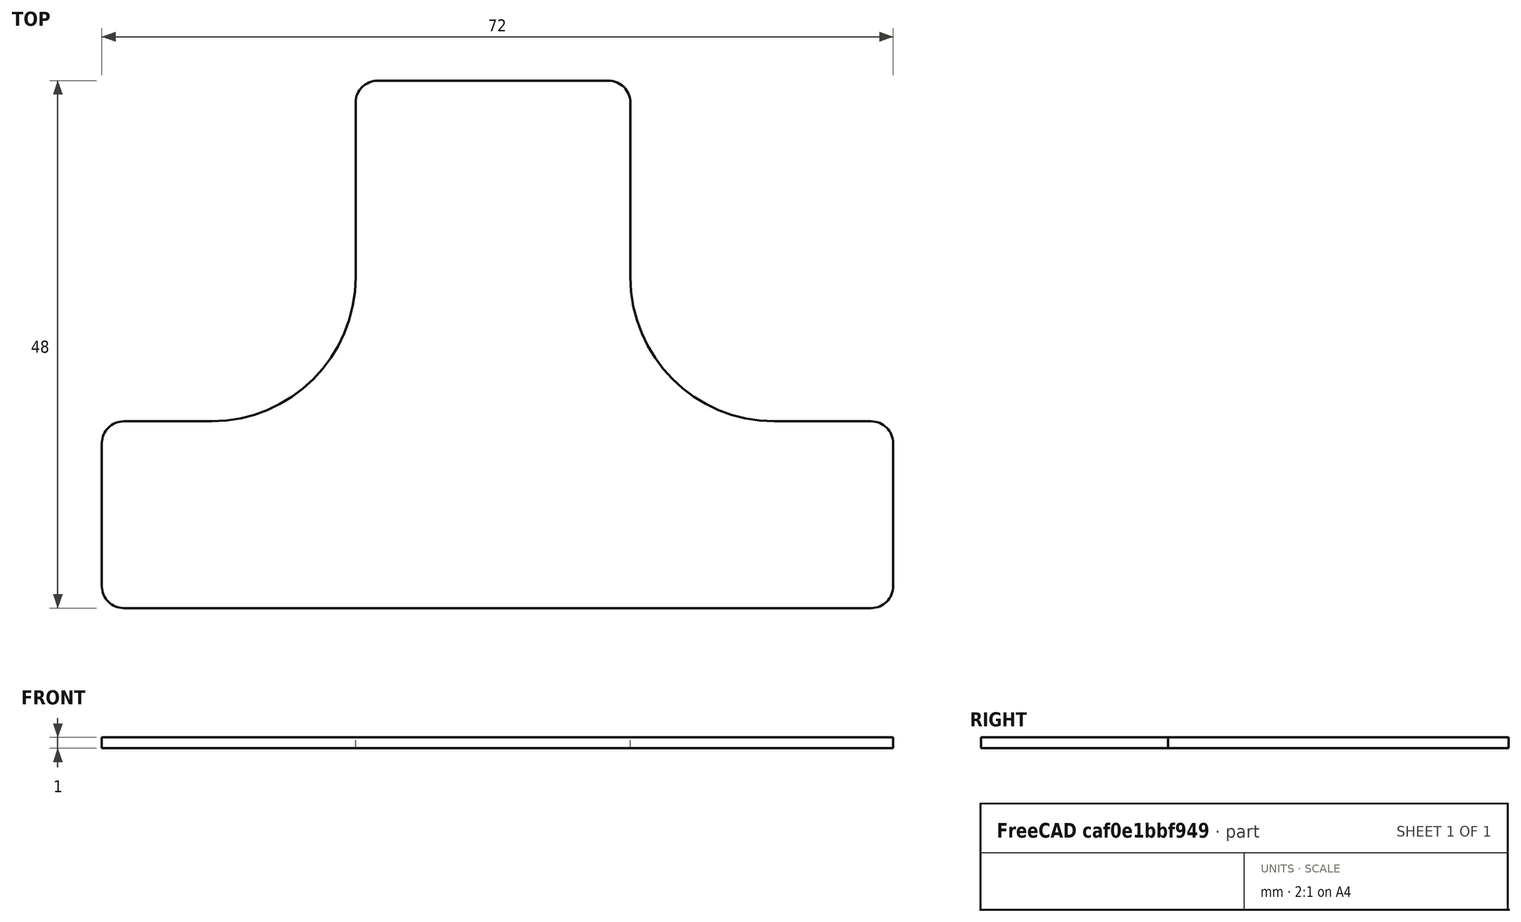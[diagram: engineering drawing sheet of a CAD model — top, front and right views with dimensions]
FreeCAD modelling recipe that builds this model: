
FCSTD DOCUMENT  (FreeCAD 0.16R6712 (Git))
Label: Me_LineFolloweArray
License: All rights reserved
LicenseURL: http://en.wikipedia.org/wiki/All_rights_reserved
objects: Sketcher::SketchObject×1, PartDesign::Pad×1
note: 3 computed .brp shape members not serialized (recipe doc carries the construction recipe); baked Part::Feature solids carry a one-line shape summary decoded from their .brp

FEATURE [Sketcher::SketchObject] Sketch
  sketch-geometry (16):
    g0: LineSegment StartX=-33.5897 StartY=-18.8788 StartZ=0 EndX=34.4103 EndY=-18.8788 EndZ=0
    g1: LineSegment StartX=-35.5897 StartY=-3.87885 StartZ=0 EndX=-35.5897 EndY=-16.8788 EndZ=0
    g2: LineSegment StartX=36.4103 StartY=-3.87885 StartZ=0 EndX=36.4103 EndY=-16.8788 EndZ=0
    g3: LineSegment StartX=-10.5 StartY=29.1212 StartZ=0 EndX=10.5 EndY=29.1212 EndZ=0
    g4: LineSegment StartX=-12.5 StartY=27.1212 StartZ=0 EndX=-12.5 EndY=11.2393 EndZ=0
    g5: LineSegment StartX=12.5 StartY=27.1212 StartZ=0 EndX=12.5 EndY=11.2393 EndZ=0
    g6: LineSegment StartX=25.6181 StartY=-1.87885 StartZ=0 EndX=34.4103 EndY=-1.87885 EndZ=0
    g7: LineSegment StartX=-33.5897 StartY=-1.87885 StartZ=0 EndX=-25.6181 EndY=-1.87885 EndZ=0
    g8: ArcOfCircle CenterX=34.4103 CenterY=-3.87885 CenterZ=0 NormalX=0 NormalY=0 NormalZ=1 Radius=2 StartAngle=0 EndAngle=1.5708
    g9: ArcOfCircle CenterX=34.4103 CenterY=-16.8788 CenterZ=0 NormalX=0 NormalY=0 NormalZ=1 Radius=2 StartAngle=4.71239 EndAngle=6.28319
    g10: ArcOfCircle CenterX=-33.5897 CenterY=-16.8788 CenterZ=0 NormalX=0 NormalY=0 NormalZ=1 Radius=2 StartAngle=3.14159 EndAngle=4.71239
    g11: ArcOfCircle CenterX=-33.5897 CenterY=-3.87885 CenterZ=0 NormalX=0 NormalY=0 NormalZ=1 Radius=2 StartAngle=1.5708 EndAngle=3.14159
    g12: ArcOfCircle CenterX=-10.5 CenterY=27.1212 CenterZ=0 NormalX=0 NormalY=0 NormalZ=1 Radius=2 StartAngle=1.5708 EndAngle=3.14159
    g13: ArcOfCircle CenterX=10.5 CenterY=27.1212 CenterZ=0 NormalX=0 NormalY=0 NormalZ=1 Radius=2 StartAngle=0 EndAngle=1.5708
    g14: ArcOfCircle CenterX=-25.6181 CenterY=11.2393 CenterZ=0 NormalX=0 NormalY=0 NormalZ=1 Radius=13.1181 StartAngle=4.71239 EndAngle=6.28319
    g15: ArcOfCircle CenterX=25.6181 CenterY=11.2393 CenterZ=0 NormalX=0 NormalY=0 NormalZ=1 Radius=13.1181 StartAngle=3.14159 EndAngle=4.71239
  constraints (36):
    c: Horizontal(g0)
    c: Vertical(g1)
    c: Vertical(g2)
    c: Horizontal(g3)
    c: Vertical(g4)
    c: Vertical(g5)
    c: Horizontal(g6)
    c: Horizontal(g7)
    c: Tangent(g2,g8) = 1.5708
    c: Tangent(g6,g8) = 1.5708
    c: Tangent(g0,g9) = -1.5708
    c: Tangent(g2,g9) = 1.5708
    c: Tangent(g0,g10) = -1.5708
    c: Tangent(g1,g10) = -1.5708
    c: Tangent(g1,g11) = -1.5708
    c: Tangent(g7,g11) = 1.5708
    c: Tangent(g3,g12) = 1.5708
    c: Tangent(g4,g12) = -1.5708
    c: Tangent(g3,g13) = 1.5708
    c: Tangent(g5,g13) = 1.5708
    c: Tangent(g4,g14) = 1.5708
    c: Tangent(g7,g14) = -1.5708
    c: Tangent(g5,g15) = -1.5708
    c: Tangent(g6,g15) = -1.5708
    c: DistanceY(g0,g7) = 17
    c: DistanceX(g1,g2) = 72
    c: DistanceX(g4,g5) = 25
    c: DistanceY(g0,g3) = 48
    c: Symmetric(g3,g3,g-2)
    c: Symmetric(g4,g5,g-2)
    c: Radius(g8) = 2
    c: Equal(g8,g9)
    c: Radius(g11) = 2
    c: Equal(g11,g10)
    c: Radius(g12) = 2
    c: DistanceY(g0,g6) = 17
FEATURE [PartDesign::Pad] Pad
  Length = 1
  Length2 = 100
  Sketch = -> Sketch
  Type = 0
